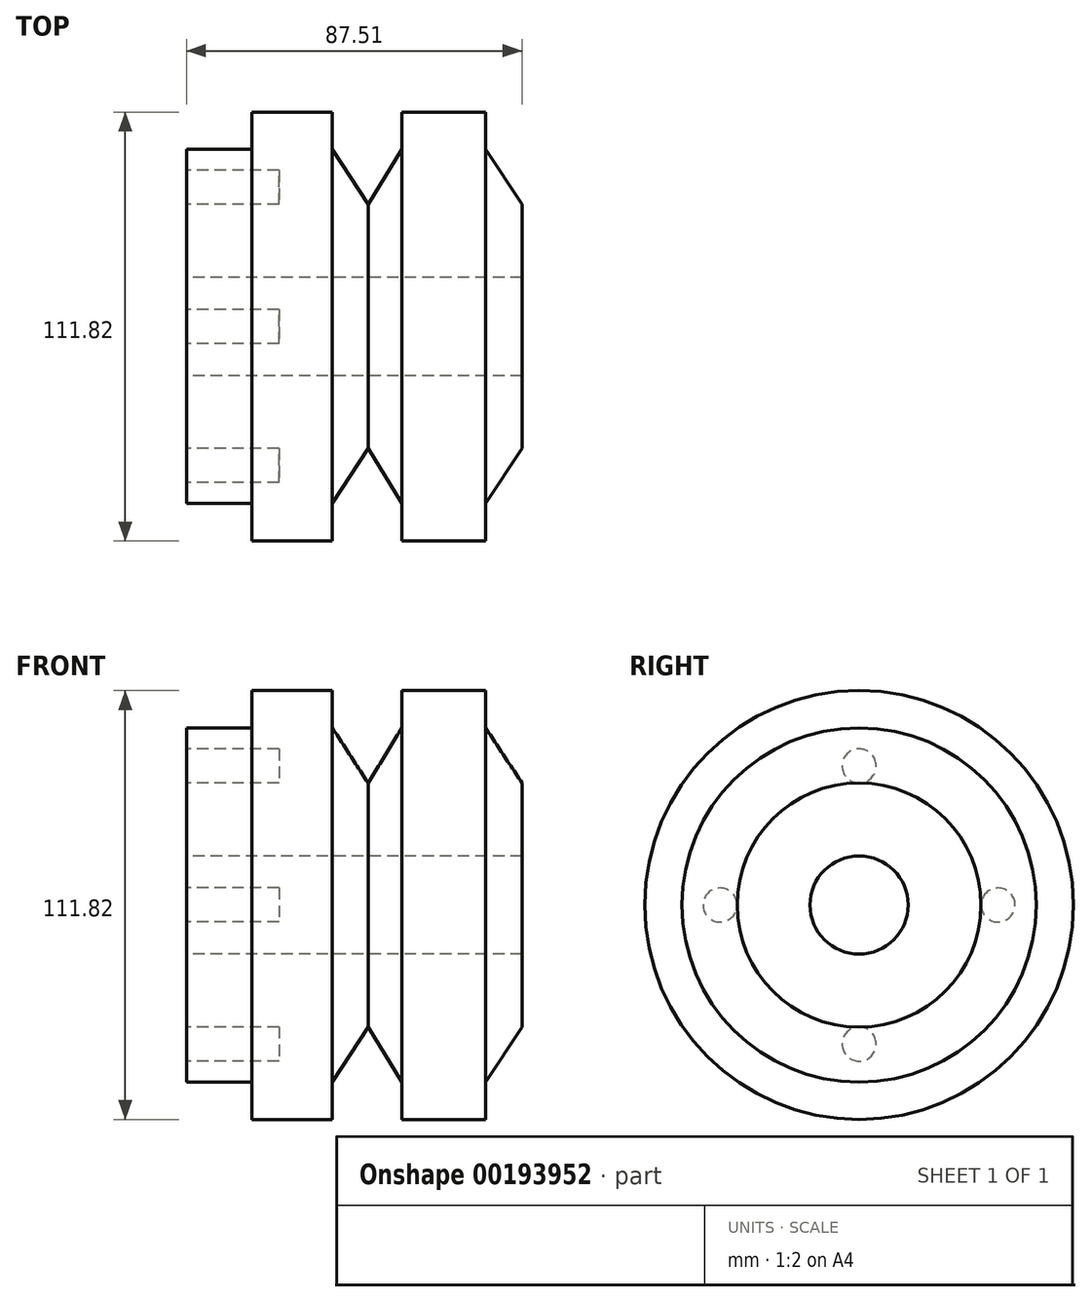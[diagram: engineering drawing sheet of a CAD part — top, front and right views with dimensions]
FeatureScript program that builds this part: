
annotation { "Feature Type Name" : "Feature", "Feature Type Description" : "" }
export const myFeature = defineFeature(function(context is Context, id is Id, definition is map)
    precondition{}
    {
        {
            var Q0;
            Q0=qCreatedBy(makeId("Front.planeOp"),FACE);
            var sketch = newSketch(context, id + "F0", { "sketchPlane" : qUnion([Q0])});
            skLineSegment(sketch, "E0", {"start": v(-47.35, 12.79) * mm, "end": v(-47.35, 46.19) * mm});
            skLineSegment(sketch, "E1", {"start": v(-47.35, 46.19) * mm, "end": v(-30.23, 46.19) * mm});
            skLineSegment(sketch, "E2", {"start": v(-30.23, 46.19) * mm, "end": v(-30.23, 55.91) * mm});
            skLineSegment(sketch, "E3", {"start": v(-30.23, 55.91) * mm, "end": v(-9.3, 55.91) * mm});
            skLineSegment(sketch, "E4", {"start": v(-9.3, 55.91) * mm, "end": v(-9.3, 46.19) * mm});
            skLineSegment(sketch, "E5", {"start": v(-9.3, 46.19) * mm, "end": v(0, 31.81) * mm});
            skLineSegment(sketch, "E6", {"start": v(0, 31.81) * mm, "end": v(8.88, 46.19) * mm});
            skLineSegment(sketch, "E7", {"start": v(8.88, 46.19) * mm, "end": v(8.88, 55.91) * mm});
            skLineSegment(sketch, "E8", {"start": v(8.88, 55.91) * mm, "end": v(30.65, 55.91) * mm});
            skLineSegment(sketch, "E9", {"start": v(30.65, 55.91) * mm, "end": v(30.65, 46.19) * mm});
            skLineSegment(sketch, "E10", {"start": v(30.65, 46.19) * mm, "end": v(40.16, 31.81) * mm});
            skLineSegment(sketch, "E11", {"start": v(40.16, 31.81) * mm, "end": v(40.16, 12.79) * mm});
            skLineSegment(sketch, "E12", {"start": v(40.16, 12.79) * mm, "end": v(-47.35, 12.79) * mm});
            skLineSegment(sketch, "E13", {"start": v(-133.8, 0) * mm, "end": v(148.4, 0) * mm, "construction": true});
            skSolve(sketch);
        }
        {
            var Q0;
            Q0 = qSketchRegion(id + "F0", true);
            var Q1;
            Q1=sQuery(id+"F0.wireOp",EDGE,"E13");
            revolve(context, id + "F1", {"entities" : qUnion([Q0]), "axis" : qUnion([Q1]), "revolveType" : RevolveType.FULL});
        }
        {
            var Q0;
            Q0=makeQuery(id+"F1.opRevolve","SWEPT_FACE",FACE,{"disambiguationData":[OSD([sQuery(id+"F0.wireOp",EDGE,"E0")])]});
            var sketch = newSketch(context, id + "F2", { "sketchPlane" : qUnion([Q0])});
            skCircle(sketch, "E14", {"center": v(0, 36.25) * mm, "radius": 4.45 * mm});
            skCircle(sketch, "E15.1.0", {"center": v(36.25, 0) * mm, "radius": 4.45 * mm});
            skCircle(sketch, "E15.2.0", {"center": v(0, -36.25) * mm, "radius": 4.45 * mm});
            skCircle(sketch, "E15.3.0", {"center": v(-36.25, 0) * mm, "radius": 4.45 * mm});
            skPoint(sketch, "E15.center", {"position": v(0, 0) * mm});
            skLineSegment(sketch, "E15.anchor1", {"start": v(0, 0) * mm, "end": v(0, 36.25) * mm, "construction": true});
            skLineSegment(sketch, "E15.anchor2", {"start": v(0, 0) * mm, "end": v(-36.25, 0) * mm, "construction": true});
            skSolve(sketch);
        }
        {
            var Q0;
            Q0 = qSketchRegion(id + "F2", true);
            extrude(context, id + "F3", {"entities" : qUnion([Q0]), "operationType" : NewBodyOperationType.REMOVE, "oppositeDirection" : true, "depth" : 24.13 * mm});
        }
    });
